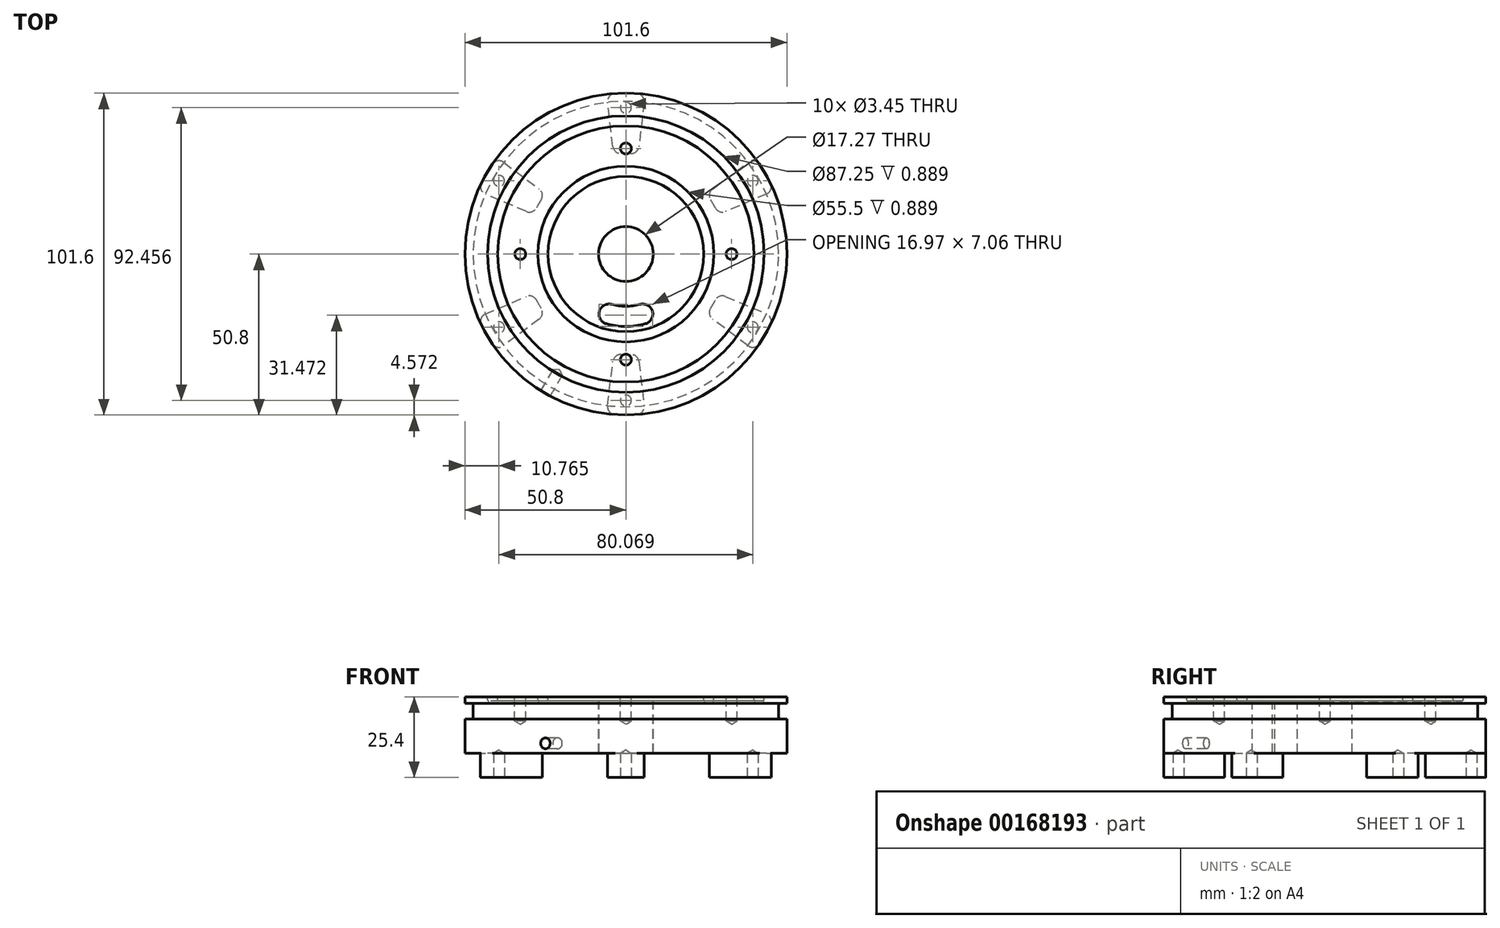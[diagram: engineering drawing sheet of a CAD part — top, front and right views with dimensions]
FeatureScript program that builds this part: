
annotation { "Feature Type Name" : "Feature", "Feature Type Description" : "" }
export const myFeature = defineFeature(function(context is Context, id is Id, definition is map)
    precondition{}
    {
        {
            var Q0;
            Q0=qCreatedBy(makeId("Top.planeOp"),FACE);
            var sketch = newSketch(context, id + "F0", { "sketchPlane" : qUnion([Q0])});
            skCircle(sketch, "E0", {"center": v(0, 0) * mm, "radius": 50.8 * mm});
            skSolve(sketch);
        }
        {
            var Q0;
            Q0=makeQuery(id+"F0.imprint","IMPRINT",FACE,{"disambiguationData":[TD([[makeQuery(id+"F0.imprint","IMPRINT",EDGE,{"derivedFrom":sQuery(id+"F0.wireOp",EDGE,"E0")}),1.0]])]});
            extrude(context, id + "F1", {"entities" : qUnion([Q0]), "depth" : 17.78 * mm});
        }
        {
            var Q0;
            Q0=makeQuery(id+"FNZgXB3MDCEPfWC_1.boolean.opBoolean","SPLIT",FACE,{"disambiguationData":[TD([makeQuery(id+"FNZgXB3MDCEPfWC_1.opExtrude","SWEPT_FACE",FACE,{"disambiguationData":[OSD([sQuery(id+"FiLk9hSRQ8Dv81E_1.wireOp",EDGE,"Xvq2NHEn-EDZK-GzOR-rNrk-moL4fFsD4KvI")])]})])],"derivedFrom":makeQuery(id+"F1.opExtrude","CAP_FACE",FACE,{"disambiguationData":[OSD([sQuery(id+"F0.wireOp",EDGE,"E0")])],"isStart":false})});
            var sketch = newSketch(context, id + "F2", { "sketchPlane" : qUnion([Q0])});
            skCircle(sketch, "E1", {"center": v(0, 0) * mm, "radius": 8.64 * mm});
            skSolve(sketch);
        }
        {
            var Q0;
            Q0=qSketchRegion(id+"F2",true);
            extrude(context, id + "F3", {"entities" : qUnion([Q0]), "operationType" : NewBodyOperationType.REMOVE, "endBound" : BoundingType.THROUGH_ALL, "oppositeDirection" : true, "depth" : 25.4 * mm});
        }
        {
            var Q0;
            Q0=makeQuery(id+"F1.opExtrude","CAP_FACE",FACE,{"disambiguationData":[OSD([sQuery(id+"F0.wireOp",EDGE,"E0")])],"isStart":true});
            var sketch = newSketch(context, id + "F4", { "sketchPlane" : qUnion([Q0])});
            skArc(sketch, "E2", {"start": v(-6.1, -50.43) * mm, "mid": v(0, -50.8) * mm, "end": v(6.1, -50.43) * mm});
            skArc(sketch, "E3", {"start": v(-3.81, -31.52) * mm, "mid": v(0, -31.75) * mm, "end": v(3.8, -31.52) * mm});
            skLineSegment(sketch, "E4", {"start": v(0, 0) * mm, "end": v(3.81, -31.52) * mm, "construction": true});
            skLineSegment(sketch, "E5", {"start": v(6.1, -50.43) * mm, "end": v(3.8, -31.52) * mm});
            skLineSegment(sketch, "E6", {"start": v(-3.8, -31.52) * mm, "end": v(-6.1, -50.43) * mm});
            skLineSegment(sketch, "E7", {"start": v(-3.81, -31.52) * mm, "end": v(3.81, -31.52) * mm, "construction": true});
            skPoint(sketch, "E8", {"position": v(0, -31.52) * mm});
            skLineSegment(sketch, "E9", {"start": v(0, 0) * mm, "end": v(-3.81, -31.52) * mm, "construction": true});
            skSolve(sketch);
        }
        {
            var Q0;
            Q0=qSketchRegion(id+"F4",true);
            extrude(context, id + "F5", {"entities" : qUnion([Q0]), "operationType" : NewBodyOperationType.ADD, "depth" : 7.62 * mm});
        }
        {
            var Q0;
            Q0=makeQuery(id+"F5.opExtrude","SWEPT_EDGE",EDGE,{"disambiguationData":[OSD([sQuery(id+"F0.wireOp",EDGE,"E0"),sQuery(id+"F4.wireOp",EDGE,"E2"),sQuery(id+"F4.wireOp",EDGE,"E5")])]});
            var Q1;
            Q1=makeQuery(id+"F5.opExtrude","SWEPT_EDGE",EDGE,{"disambiguationData":[OSD([sQuery(id+"F4.wireOp",EDGE,"E3"),sQuery(id+"F4.wireOp",EDGE,"E5")])]});
            var Q2;
            Q2=makeQuery(id+"F5.opExtrude","SWEPT_EDGE",EDGE,{"disambiguationData":[OSD([sQuery(id+"F0.wireOp",EDGE,"E0"),sQuery(id+"F4.wireOp",EDGE,"E2"),sQuery(id+"F4.wireOp",EDGE,"sxsrdx0H-xiQs-OsdF-6Z6r-2XBd8uqwUAgb")])]});
            var Q3;
            Q3=makeQuery(id+"F5.opExtrude","SWEPT_EDGE",EDGE,{"disambiguationData":[OSD([sQuery(id+"F4.wireOp",EDGE,"E3"),sQuery(id+"F4.wireOp",EDGE,"sxsrdx0H-xiQs-OsdF-6Z6r-2XBd8uqwUAgb")])]});
            fillet(context, id + "F6", {"entities" : qUnion([Q0, Q1, Q2, Q3]), "radius" : 2.54 * mm, "tangentPropagation" : true, "allowEdgeOverflow" : false});
        }
        {
            var Q0;
            Q0=makeQuery(id+"F5.opExtrude","CAP_FACE",FACE,{"disambiguationData":[OSD([sQuery(id+"F4.wireOp",EDGE,"E2"),sQuery(id+"F4.wireOp",EDGE,"E3"),sQuery(id+"F4.wireOp",EDGE,"E5"),sQuery(id+"F4.wireOp",EDGE,"sxsrdx0H-xiQs-OsdF-6Z6r-2XBd8uqwUAgb")])],"isStart":false});
            var sketch = newSketch(context, id + "F7", { "sketchPlane" : qUnion([Q0])});
            skLineSegment(sketch, "E10", {"start": v(0, 0) * mm, "end": v(0, 0) * mm});
            skLineSegment(sketch, "E11", {"start": v(0, 0) * mm, "end": v(0, -50.68) * mm, "construction": true});
            skPoint(sketch, "E12.3.0", {"position": v(0, -46.23) * mm});
            skPoint(sketch, "E12.center", {"position": v(0, 0) * mm});
            skPoint(sketch, "E13.1.0", {"position": v(40.03, -23.11) * mm});
            skPoint(sketch, "E13.2.0", {"position": v(40.03, 23.11) * mm});
            skPoint(sketch, "E14.0.3.0", {"position": v(0, 46.23) * mm});
            skPoint(sketch, "E14.0.4.0", {"position": v(-40.03, 23.11) * mm});
            skPoint(sketch, "E14.0.5.0", {"position": v(-40.03, -23.11) * mm});
            skSolve(sketch);
        }
        {
            var Q0;
            Q0=makeQuery(id+"F1.opExtrude","SWEPT_BODY",BODY,{"disambiguationData":[OSD([sQuery(id+"F0.wireOp",EDGE,"E0")])]});
            var Q1;
            Q1=makeQuery(id+"F3.boolean.opBoolean","COPY",FACE,{"derivedFrom":makeQuery(id+"F3.opExtrude","SWEPT_FACE",FACE,{"disambiguationData":[OSD([sQuery(id+"F2.wireOp",EDGE,"E1")])]})});
            circularPattern(context, id + "F8", {"operationType" : NewBodyOperationType.ADD, "entities" : qUnion([Q0]), "axis" : qUnion([Q1]), "angle" : 360 * degree, "instanceCount" : 6, "equalSpace" : true});
        }
        {
            var Q0;
            Q0=sQuery(id+"F7.wireOp",VERTEX,"E12.3.0");
            var Q1;
            Q1=sQuery(id+"F7.wireOp",VERTEX,"E13.1.0");
            var Q2;
            Q2=sQuery(id+"F7.wireOp",VERTEX,"E13.2.0");
            var Q3;
            Q3=sQuery(id+"F7.wireOp",VERTEX,"E14.0.3.0");
            var Q4;
            Q4=sQuery(id+"F7.wireOp",VERTEX,"E14.0.4.0");
            var Q5;
            Q5=sQuery(id+"F7.wireOp",VERTEX,"E14.0.5.0");
            var Q6;
            Q6=makeQuery(id+"F1.opExtrude","SWEPT_BODY",BODY,{"disambiguationData":[OSD([sQuery(id+"F0.wireOp",EDGE,"E0")])]});
            hole(context, id + "F9", {"style" : HoleStyle.SIMPLE, "endStyle" : HoleEndStyle.BLIND, "standardTappedOrClearance" : lookupTablePath({ "standard" : "ANSI", "engagement" : "75%", "pitch" : "32 tpi", "size" : "#8", "type" : "Tapped" }), "standardBlindInLast" : lookupTablePath({ "standard" : "ANSI", "engagement" : "75%", "pitch" : "32 tpi", "size" : "#8", "type" : "Tapped" }), "holeDiameter" : 3.45 * mm, "holeDepth" : 7.62 * mm, "locations" : qUnion([Q0, Q1, Q2, Q3, Q4, Q5]), "scope" : qUnion([Q6]), "majorDiameter" : 4.17 * mm});
        }
        {
            var Q0;
            {var subQ0=sQuery(id+"F0.wireOp",EDGE,"E0");Q0=makeQuery(id+"FNZgXB3MDCEPfWC_1.boolean.opBoolean","SPLIT",FACE,{"disambiguationData":[TD([makeQuery(id+"F1.opExtrude","SWEPT_FACE",FACE,{"disambiguationData":[OSD([subQ0])]})])],"derivedFrom":makeQuery(id+"F1.opExtrude","CAP_FACE",FACE,{"disambiguationData":[OSD([subQ0])],"isStart":false})});}
            var sketch = newSketch(context, id + "F10", { "sketchPlane" : qUnion([Q0])});
            skCircle(sketch, "E15", {"center": v(0, 0) * mm, "radius": 42.02 * mm, "construction": true});
            skCircle(sketch, "E16", {"center": v(0, 0) * mm, "radius": 40.42 * mm});
            skCircle(sketch, "E17", {"center": v(0, 0) * mm, "radius": 43.62 * mm});
            skSolve(sketch);
        }
        {
            var Q0;
            Q0=qSketchRegion(id+"F10",true);
            extrude(context, id + "F11", {"entities" : qUnion([Q0]), "operationType" : NewBodyOperationType.REMOVE, "oppositeDirection" : true, "depth" : 1.3 * mm});
        }
        {
            var Q0;
            Q0=makeQuery(id+"F11.boolean.opBoolean","COPY",EDGE,{"derivedFrom":makeQuery(id+"F11.opExtrude","CAP_EDGE",EDGE,{"disambiguationData":[OSD([sQuery(id+"F10.wireOp",EDGE,"E17")])],"isStart":false})});
            var Q1;
            Q1=makeQuery(id+"F11.boolean.opBoolean","COPY",EDGE,{"derivedFrom":makeQuery(id+"F11.opExtrude","CAP_EDGE",EDGE,{"disambiguationData":[OSD([sQuery(id+"F10.wireOp",EDGE,"E16")])],"isStart":false})});
            fillet(context, id + "F12", {"entities" : qUnion([Q0, Q1]), "radius" : 0.4 * mm, "tangentPropagation" : true, "allowEdgeOverflow" : false});
        }
        {
            var Q0;
            Q0=makeQuery(id+"F11.boolean.opBoolean","SPLIT",FACE,{"disambiguationData":[TD([makeQuery(id+"F3.boolean.opBoolean","COPY",FACE,{"derivedFrom":makeQuery(id+"F3.opExtrude","SWEPT_FACE",FACE,{"disambiguationData":[OSD([sQuery(id+"F2.wireOp",EDGE,"E1")])]})})])],"derivedFrom":makeQuery(id+"F1.opExtrude","CAP_FACE",FACE,{"disambiguationData":[OSD([sQuery(id+"F0.wireOp",EDGE,"E0")])],"isStart":false})});
            var sketch = newSketch(context, id + "F13", { "sketchPlane" : qUnion([Q0])});
            skCircle(sketch, "E18", {"center": v(0, 0) * mm, "radius": 26.15 * mm, "construction": true});
            skCircle(sketch, "E19", {"center": v(0, 0) * mm, "radius": 24.55 * mm});
            skCircle(sketch, "E20", {"center": v(0, 0) * mm, "radius": 27.75 * mm});
            skSolve(sketch);
        }
        {
            var Q0;
            Q0=qSketchRegion(id+"F13",true);
            extrude(context, id + "F14", {"entities" : qUnion([Q0]), "operationType" : NewBodyOperationType.REMOVE, "oppositeDirection" : true, "depth" : 1.3 * mm});
        }
        {
            var Q0;
            Q0=makeQuery(id+"F14.boolean.opBoolean","COPY",EDGE,{"derivedFrom":makeQuery(id+"F14.opExtrude","CAP_EDGE",EDGE,{"disambiguationData":[OSD([sQuery(id+"F13.wireOp",EDGE,"E20")])],"isStart":false})});
            var Q1;
            Q1=makeQuery(id+"F14.boolean.opBoolean","COPY",EDGE,{"derivedFrom":makeQuery(id+"F14.opExtrude","CAP_EDGE",EDGE,{"disambiguationData":[OSD([sQuery(id+"F13.wireOp",EDGE,"E19")])],"isStart":false})});
            fillet(context, id + "F15", {"entities" : qUnion([Q0, Q1]), "radius" : 0.4 * mm, "tangentPropagation" : true, "allowEdgeOverflow" : false});
        }
        {
            var Q0;
            {var subQ0=makeQuery(id+"F3.boolean.opBoolean","COPY",FACE,{"derivedFrom":makeQuery(id+"F3.opExtrude","SWEPT_FACE",FACE,{"disambiguationData":[OSD([sQuery(id+"F2.wireOp",EDGE,"E1")])]})});Q0=makeQuery(id+"F14.boolean.opBoolean","SPLIT",FACE,{"disambiguationData":[TD([subQ0])],"derivedFrom":makeQuery(id+"F11.boolean.opBoolean","SPLIT",FACE,{"disambiguationData":[TD([subQ0])],"derivedFrom":makeQuery(id+"F1.opExtrude","CAP_FACE",FACE,{"disambiguationData":[OSD([sQuery(id+"F0.wireOp",EDGE,"E0")])],"isStart":false})})});}
            var sketch = newSketch(context, id + "F16", { "sketchPlane" : qUnion([Q0])});
            skLineSegment(sketch, "E21", {"start": v(0, 0) * mm, "end": v(6.98, -14.96) * mm, "construction": true});
            skArc(sketch, "E22", {"start": v(6.98, -14.96) * mm, "mid": v(0, -16.51) * mm, "end": v(-6.98, -14.96) * mm});
            skArc(sketch, "E23", {"start": v(9.66, -20.72) * mm, "mid": v(0, -22.86) * mm, "end": v(-9.66, -20.72) * mm});
            skLineSegment(sketch, "E24", {"start": v(-9.66, -20.72) * mm, "end": v(-6.98, -14.96) * mm});
            skLineSegment(sketch, "E25", {"start": v(0, 0) * mm, "end": v(-6.98, -14.96) * mm, "construction": true});
            skLineSegment(sketch, "E26", {"start": v(9.66, -20.72) * mm, "end": v(6.98, -14.96) * mm});
            skLineSegment(sketch, "E27", {"start": v(0, -16.51) * mm, "end": v(0, 0) * mm, "construction": true});
            skSolve(sketch);
        }
        {
            var Q0;
            Q0=qSketchRegion(id+"F16",true);
            extrude(context, id + "F17", {"entities" : qUnion([Q0]), "operationType" : NewBodyOperationType.REMOVE, "endBound" : BoundingType.THROUGH_ALL, "oppositeDirection" : true, "depth" : 25.4 * mm});
        }
        {
            var Q0;
            Q0=makeQuery(id+"F17.boolean.opBoolean","COPY",EDGE,{"derivedFrom":makeQuery(id+"F17.opExtrude","SWEPT_EDGE",EDGE,{"disambiguationData":[OSD([sQuery(id+"F16.wireOp",EDGE,"E22"),sQuery(id+"F16.wireOp",EDGE,"E24")])]})});
            var Q1;
            Q1=makeQuery(id+"F17.boolean.opBoolean","COPY",EDGE,{"derivedFrom":makeQuery(id+"F17.opExtrude","SWEPT_EDGE",EDGE,{"disambiguationData":[OSD([sQuery(id+"F16.wireOp",EDGE,"E23"),sQuery(id+"F16.wireOp",EDGE,"E24")])]})});
            var Q2;
            Q2=makeQuery(id+"F17.boolean.opBoolean","COPY",EDGE,{"derivedFrom":makeQuery(id+"F17.opExtrude","SWEPT_EDGE",EDGE,{"disambiguationData":[OSD([sQuery(id+"F16.wireOp",EDGE,"E22"),sQuery(id+"F16.wireOp",EDGE,"nJm0js4g-YAOA-XNub-Ppl5-B8IrQimasCNu")])]})});
            var Q3;
            Q3=makeQuery(id+"F17.boolean.opBoolean","COPY",EDGE,{"derivedFrom":makeQuery(id+"F17.opExtrude","SWEPT_EDGE",EDGE,{"disambiguationData":[OSD([sQuery(id+"F16.wireOp",EDGE,"E23"),sQuery(id+"F16.wireOp",EDGE,"nJm0js4g-YAOA-XNub-Ppl5-B8IrQimasCNu")])]})});
            fillet(context, id + "F18", {"entities" : qUnion([Q0, Q1, Q2, Q3]), "radius" : 3.17 * mm, "tangentPropagation" : true, "allowEdgeOverflow" : false});
        }
        {
            var Q0;
            {var subQ0=makeQuery(id+"F11.opExtrude","SWEPT_FACE",FACE,{"disambiguationData":[OSD([sQuery(id+"F10.wireOp",EDGE,"E16")])]});Q0=makeQuery(id+"F14.boolean.opBoolean","SPLIT",FACE,{"disambiguationData":[TD([makeQuery(id+"F11.boolean.opBoolean","COPY",FACE,{"derivedFrom":subQ0})])],"derivedFrom":makeQuery(id+"F11.boolean.opBoolean","SPLIT",FACE,{"disambiguationData":[TD([makeQuery(id+"F3.boolean.opBoolean","COPY",FACE,{"derivedFrom":makeQuery(id+"F3.opExtrude","SWEPT_FACE",FACE,{"disambiguationData":[OSD([sQuery(id+"F2.wireOp",EDGE,"E1")])]})})])],"derivedFrom":makeQuery(id+"F1.opExtrude","CAP_FACE",FACE,{"disambiguationData":[OSD([sQuery(id+"F0.wireOp",EDGE,"E0")])],"isStart":false})})});}
            var sketch = newSketch(context, id + "F19", { "sketchPlane" : qUnion([Q0])});
            skCircle(sketch, "E28", {"center": v(0, 0) * mm, "radius": 33.34 * mm, "construction": true});
            skLineSegment(sketch, "E29", {"start": v(0, 0) * mm, "end": v(0, -33.34) * mm, "construction": true});
            skPoint(sketch, "E30", {"position": v(0, -33.34) * mm});
            skPoint(sketch, "E31", {"position": v(-33.34, 0) * mm});
            skPoint(sketch, "E32", {"position": v(33.34, 0) * mm});
            skPoint(sketch, "E33", {"position": v(0, 33.34) * mm});
            skSolve(sketch);
        }
        {
            var Q0;
            {var subQ1=sQuery(id+"F0.wireOp",EDGE,"E0");var subQ2=makeQuery(id+"F1.opExtrude","SWEPT_FACE",FACE,{"disambiguationData":[OSD([subQ1])]});Q0=makeQuery(id+"F11.boolean.opBoolean","SPLIT",FACE,{"disambiguationData":[TD([subQ2])],"derivedFrom":makeQuery(id+"F1.opExtrude","CAP_FACE",FACE,{"disambiguationData":[OSD([subQ1])],"isStart":false})});}
            cPlane(context, id + "F20", {"entities" : qUnion([Q0]), "cplaneType" : CPlaneType.OFFSET, "offset" : 2.03 * mm, "oppositeDirection" : true, "width" : 152.4 * mm, "height" : 152.4 * mm});
        }
        {
            var Q0;
            Q0=qCreatedBy(id+"F20.planeOp",FACE);
            var sketch = newSketch(context, id + "F21", { "sketchPlane" : qUnion([Q0])});
            skCircle(sketch, "E34", {"center": v(0, 0) * mm, "radius": 48.2 * mm});
            skCircle(sketch, "E35.0", {"center": v(0, 0) * mm, "radius": 50.8 * mm});
            skSolve(sketch);
        }
        {
            var Q0;
            Q0=qSketchRegion(id+"F21",true);
            extrude(context, id + "F22", {"entities" : qUnion([Q0]), "operationType" : NewBodyOperationType.REMOVE, "oppositeDirection" : true, "depth" : 5 * mm});
        }
        {
            var Q0;
            Q0=makeQuery(id+"F22.boolean.opBoolean","COPY",EDGE,{"derivedFrom":makeQuery(id+"F22.opExtrude","CAP_EDGE",EDGE,{"disambiguationData":[OSD([sQuery(id+"F21.wireOp",EDGE,"E34")])],"isStart":false})});
            var Q1;
            Q1=makeQuery(id+"F22.boolean.opBoolean","COPY",EDGE,{"derivedFrom":makeQuery(id+"F22.opExtrude","CAP_EDGE",EDGE,{"disambiguationData":[OSD([sQuery(id+"F21.wireOp",EDGE,"E34")])],"isStart":true})});
            fillet(context, id + "F23", {"entities" : qUnion([Q0, Q1]), "radius" : 0.76 * mm, "tangentPropagation" : true, "allowEdgeOverflow" : false});
        }
        {
            var Q0;
            {var subQ1=sQuery(id+"F0.wireOp",EDGE,"E0");var subQ2=makeQuery(id+"F1.opExtrude","SWEPT_FACE",FACE,{"disambiguationData":[OSD([subQ1])]});Q0=makeQuery(id+"F11.boolean.opBoolean","SPLIT",FACE,{"disambiguationData":[TD([subQ2])],"derivedFrom":makeQuery(id+"F1.opExtrude","CAP_FACE",FACE,{"disambiguationData":[OSD([subQ1])],"isStart":false})});}
            var sketch = newSketch(context, id + "F24", { "sketchPlane" : qUnion([Q0])});
            skCircle(sketch, "E36.0", {"center": v(0, 0) * mm, "radius": 50.8 * mm, "construction": true});
            skPoint(sketch, "E37", {"position": v(-25.4, -44) * mm});
            skLineSegment(sketch, "E38", {"start": v(0, -50.8) * mm, "end": v(0, 0) * mm, "construction": true});
            skLineSegment(sketch, "E39", {"start": v(0, 0) * mm, "end": v(-17.96, -31.1) * mm, "construction": true});
            skLineSegment(sketch, "E40", {"start": v(-17.96, -31.1) * mm, "end": v(-25.4, -44) * mm, "construction": true});
            skSolve(sketch);
        }
        {
            var Q0;
            Q0=qCreatedBy(makeId("Front.planeOp"),FACE);
            var sketch = newSketch(context, id + "F25", { "sketchPlane" : qUnion([Q0])});
            skLineSegment(sketch, "E41", {"start": v(0, 0) * mm, "end": v(0, 38.57) * mm, "construction": true});
            skSolve(sketch);
        }
        {
            var Q0;
            Q0=sQuery(id+"F25.wireOp",EDGE,"E41");
            cPlane(context, id + "F26", {"entities" : qUnion([Q0]), "cplaneType" : CPlaneType.LINE_ANGLE, "offset" : 25.4 * mm, "angle" : 60 * degree, "width" : 152.4 * mm, "height" : 152.4 * mm});
        }
        {
            var Q0;
            Q0=sQuery(id+"F24.wireOp",VERTEX,"E37");
            var Q1;
            Q1=qCreatedBy(id+"F26.planeOp",FACE);
            cPlane(context, id + "F27", {"entities" : qUnion([Q0, Q1]), "cplaneType" : CPlaneType.PLANE_POINT, "offset" : 25.4 * mm, "width" : 152.4 * mm, "height" : 152.4 * mm});
        }
        {
            var Q0;
            Q0=qCreatedBy(id+"F27.planeOp",FACE);
            var sketch = newSketch(context, id + "F28", { "sketchPlane" : qUnion([Q0])});
            skLineSegment(sketch, "E42", {"start": v(0, 0) * mm, "end": v(0, 3.12) * mm, "construction": true});
            skPoint(sketch, "E43", {"position": v(0, 3.12) * mm});
            skSolve(sketch);
        }
        {
            var Q0;
            Q0=sQuery(id+"F28.wireOp",VERTEX,"E43");
            var Q1;
            Q1=makeQuery(id+"F1.opExtrude","SWEPT_BODY",BODY,{"disambiguationData":[OSD([sQuery(id+"F0.wireOp",EDGE,"E0")])]});
            hole(context, id + "F29", {"style" : HoleStyle.SIMPLE, "endStyle" : HoleEndStyle.BLIND, "oppositeDirection" : true, "standardTappedOrClearance" : lookupTablePath({ "standard" : "ANSI", "engagement" : "75%", "pitch" : "32 tpi", "size" : "#8", "type" : "Tapped" }), "standardBlindInLast" : lookupTablePath({ "standard" : "ANSI", "engagement" : "75%", "pitch" : "32 tpi", "size" : "#8", "type" : "Tapped" }), "holeDiameter" : 3.45 * mm, "holeDepth" : 7.62 * mm, "locations" : qUnion([Q0]), "scope" : qUnion([Q1]), "majorDiameter" : 4.17 * mm});
        }
        {
            var Q0;
            Q0=sQuery(id+"F19.wireOp",VERTEX,"E31");
            var Q1;
            Q1=sQuery(id+"F19.wireOp",VERTEX,"E33");
            var Q2;
            Q2=sQuery(id+"F19.wireOp",VERTEX,"E32");
            var Q3;
            Q3=sQuery(id+"F19.wireOp",VERTEX,"E30");
            var Q4;
            Q4=makeQuery(id+"F1.opExtrude","SWEPT_BODY",BODY,{"disambiguationData":[OSD([sQuery(id+"F0.wireOp",EDGE,"E0")])]});
            hole(context, id + "F30", {"style" : HoleStyle.SIMPLE, "endStyle" : HoleEndStyle.BLIND, "standardTappedOrClearance" : lookupTablePath({ "standard" : "ANSI", "engagement" : "75%", "pitch" : "32 tpi", "size" : "#8", "type" : "Tapped" }), "standardBlindInLast" : lookupTablePath({ "standard" : "ANSI", "engagement" : "75%", "pitch" : "32 tpi", "size" : "#8", "type" : "Tapped" }), "holeDiameter" : 3.45 * mm, "holeDepth" : 7.62 * mm, "locations" : qUnion([Q0, Q1, Q2, Q3]), "scope" : qUnion([Q4]), "majorDiameter" : 4.17 * mm});
        }
    });
